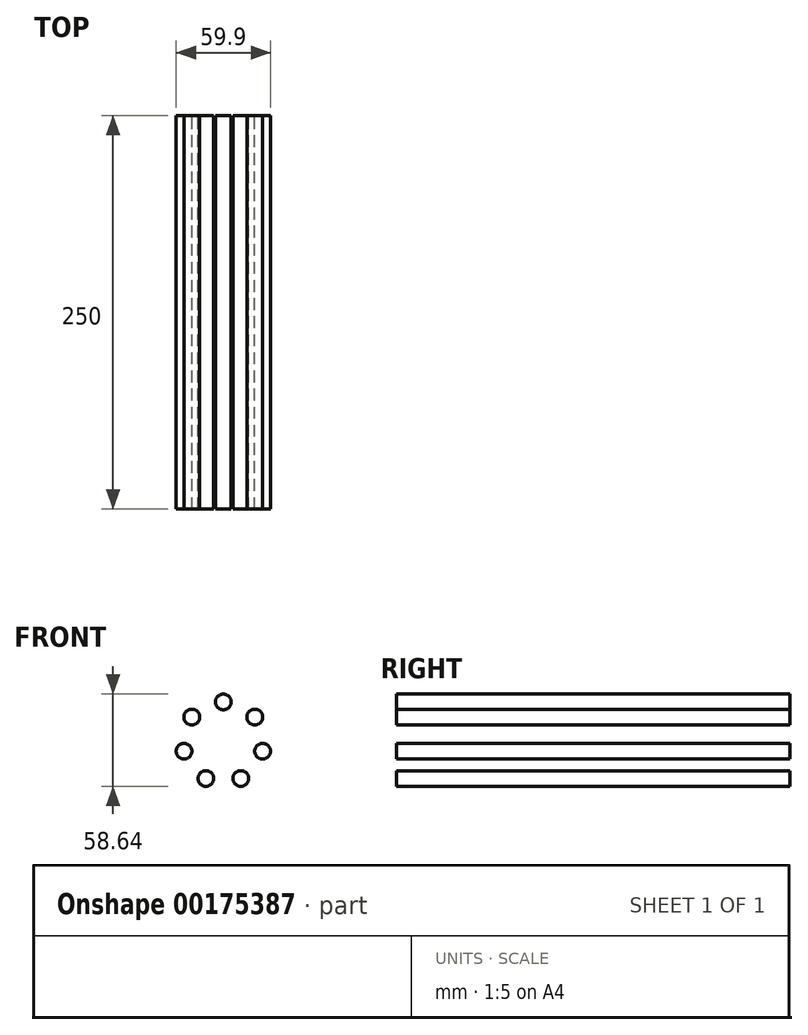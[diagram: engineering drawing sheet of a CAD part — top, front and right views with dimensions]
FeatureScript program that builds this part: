
annotation { "Feature Type Name" : "Feature", "Feature Type Description" : "" }
export const myFeature = defineFeature(function(context is Context, id is Id, definition is map)
    precondition{}
    {
        {
            var Q0;
            Q0=qCreatedBy(makeId("Front.planeOp"),FACE);
            var sketch = newSketch(context, id + "F0", { "sketchPlane" : qUnion([Q0])});
            skCircle(sketch, "E0.cCircle", {"center": v(0, 0) * mm, "radius": 25.59 * mm, "construction": true});
            skLineSegment(sketch, "E0.0", {"start": v(25.59, 0) * mm, "end": v(18.1, -18.1) * mm, "construction": true});
            skLineSegment(sketch, "E0.1", {"start": v(18.1, -18.1) * mm, "end": v(0, -25.59) * mm, "construction": true});
            skLineSegment(sketch, "E0.2", {"start": v(0, -25.59) * mm, "end": v(-18.1, -18.1) * mm, "construction": true});
            skLineSegment(sketch, "E0.3", {"start": v(-18.1, -18.1) * mm, "end": v(-25.59, 0) * mm, "construction": true});
            skLineSegment(sketch, "E0.4", {"start": v(-25.59, 0) * mm, "end": v(-18.1, 18.1) * mm, "construction": true});
            skLineSegment(sketch, "E0.5", {"start": v(-18.1, 18.1) * mm, "end": v(0, 25.59) * mm, "construction": true});
            skLineSegment(sketch, "E0.6", {"start": v(0, 25.59) * mm, "end": v(18.1, 18.1) * mm, "construction": true});
            skLineSegment(sketch, "E0.7", {"start": v(18.1, 18.1) * mm, "end": v(25.59, 0) * mm, "construction": true});
            skCircle(sketch, "E1", {"center": v(0, 25.59) * mm, "radius": 5 * mm});
            skCircle(sketch, "E2.1.0", {"center": v(20, 15.95) * mm, "radius": 5 * mm});
            skCircle(sketch, "E2.2.0", {"center": v(24.95, -5.7) * mm, "radius": 5 * mm});
            skCircle(sketch, "E2.3.0", {"center": v(11.1, -23.05) * mm, "radius": 5 * mm});
            skCircle(sketch, "E2.4.0", {"center": v(-11.1, -23.05) * mm, "radius": 5 * mm});
            skCircle(sketch, "E2.5.0", {"center": v(-24.95, -5.7) * mm, "radius": 5 * mm});
            skCircle(sketch, "E2.6.0", {"center": v(-20, 15.95) * mm, "radius": 5 * mm});
            skLineSegment(sketch, "E2.anchor1", {"start": v(0, 0) * mm, "end": v(0, 25.59) * mm, "construction": true});
            skLineSegment(sketch, "E2.anchor2", {"start": v(0, 0) * mm, "end": v(0, 25.59) * mm, "construction": true});
            skSolve(sketch);
        }
        {
            var Q0;
            Q0 = qSketchRegion(id + "F0", true);
            extrude(context, id + "F1", {"entities" : qUnion([Q0]), "depth" : 250 * mm});
        }
    });
